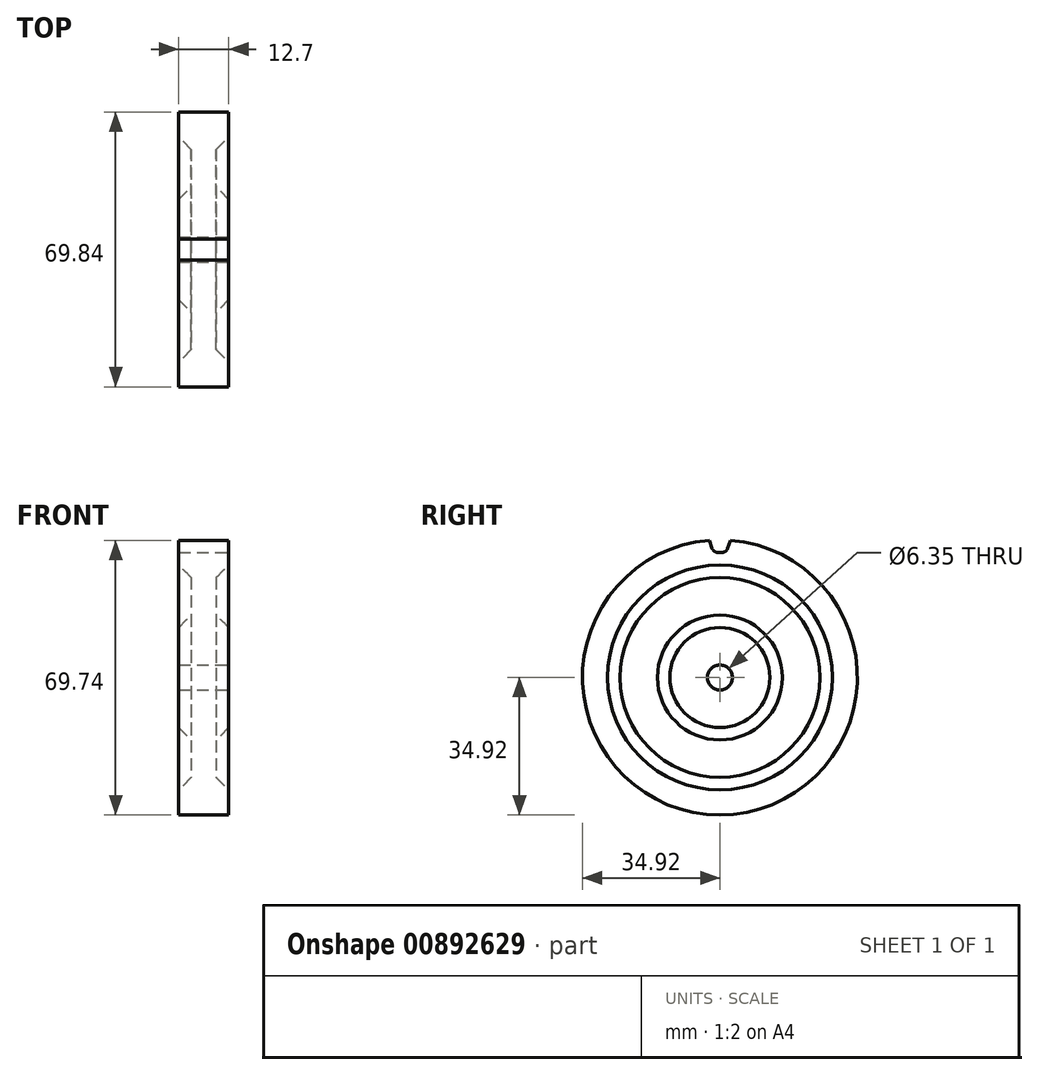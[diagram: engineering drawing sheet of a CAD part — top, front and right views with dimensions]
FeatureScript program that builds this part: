
annotation { "Feature Type Name" : "Feature", "Feature Type Description" : "" }
export const myFeature = defineFeature(function(context is Context, id is Id, definition is map)
    precondition{}
    {
        {
            var Q0;
            Q0=qCreatedBy(makeId("Front.planeOp"),FACE);
            var sketch = newSketch(context, id + "F0", { "sketchPlane" : qUnion([Q0])});
            skLineSegment(sketch, "E0", {"start": v(0, -32.59) * mm, "end": v(0, 41.72) * mm, "construction": true});
            skLineSegment(sketch, "E1", {"start": v(0, 34.93) * mm, "end": v(6.35, 34.93) * mm});
            skLineSegment(sketch, "E2", {"start": v(6.35, 34.93) * mm, "end": v(6.35, 28.58) * mm});
            skLineSegment(sketch, "E3", {"start": v(6.35, 28.58) * mm, "end": v(3.17, 25.4) * mm});
            skLineSegment(sketch, "E4", {"start": v(3.17, 25.4) * mm, "end": v(3.17, 15.88) * mm});
            skLineSegment(sketch, "E5", {"start": v(3.17, 15.88) * mm, "end": v(6.35, 12.7) * mm});
            skLineSegment(sketch, "E6", {"start": v(6.35, 12.7) * mm, "end": v(6.35, 0) * mm});
            skLineSegment(sketch, "E7", {"start": v(-34.52, 0) * mm, "end": v(33.25, 0) * mm, "construction": true});
            skLineSegment(sketch, "E8.MirrorCS", {"start": v(-6.35, 12.7) * mm, "end": v(-6.35, 0) * mm});
            skLineSegment(sketch, "E9.MirrorCS", {"start": v(-6.35, 34.93) * mm, "end": v(-6.35, 28.58) * mm});
            skLineSegment(sketch, "E10.MirrorCS", {"start": v(-3.17, 25.4) * mm, "end": v(-3.17, 15.88) * mm});
            skLineSegment(sketch, "E11.MirrorCS", {"start": v(-6.35, 28.58) * mm, "end": v(-3.17, 25.4) * mm});
            skLineSegment(sketch, "E12.MirrorCS", {"start": v(-3.17, 15.88) * mm, "end": v(-6.35, 12.7) * mm});
            skLineSegment(sketch, "E13.MirrorCS", {"start": v(0, 34.93) * mm, "end": v(-6.35, 34.93) * mm});
            skLineSegment(sketch, "E14", {"start": v(-6.35, 0) * mm, "end": v(6.35, 0) * mm});
            skSolve(sketch);
        }
        {
            var Q0;
            Q0=qSketchRegion(id+"F0",true);
            var Q1;
            Q1=sQuery(id+"F0.wireOp",EDGE,"E7");
            revolve(context, id + "F1", {"surfaceOperationType" : NewSurfaceOperationType.NEW, "entities" : qUnion([Q0]), "axis" : qUnion([Q1]), "revolveType" : RevolveType.FULL});
        }
        {
            var Q0;
            Q0=makeQuery(id+"F1.opRevolve","SWEPT_FACE",FACE,{"disambiguationData":[OSD([sQuery(id+"F0.wireOp",EDGE,"E6")])]});
            var sketch = newSketch(context, id + "F2", { "sketchPlane" : qUnion([Q0])});
            skCircle(sketch, "E15", {"center": v(0, 0) * mm, "radius": 3.18 * mm});
            skSolve(sketch);
        }
        {
            var Q0;
            Q0=makeQuery(id+"F2.imprint","IMPRINT",FACE,{"disambiguationData":[TD([[makeQuery(id+"F2.imprint","IMPRINT",EDGE,{"derivedFrom":sQuery(id+"F2.wireOp",EDGE,"E15")}),1.0]])]});
            extrude(context, id + "F3", {"entities" : qUnion([Q0]), "operationType" : NewBodyOperationType.REMOVE, "endBound" : BoundingType.THROUGH_ALL, "oppositeDirection" : true, "depth" : 25.4 * mm, "offsetDistance" : 25.4 * mm});
        }
        {
            var Q0;
            Q0=makeQuery(id+"F1.opRevolve","SWEPT_FACE",FACE,{"disambiguationData":[OSD([sQuery(id+"F0.wireOp",EDGE,"E2")])]});
            var sketch = newSketch(context, id + "F4", { "sketchPlane" : qUnion([Q0])});
            skLineSegment(sketch, "E16", {"start": v(0, 0) * mm, "end": v(0, 48.24) * mm, "construction": true});
            skArc(sketch, "E17.0", {"start": v(2.7, 34.82) * mm, "mid": v(0, 34.92) * mm, "end": v(-2.7, 34.82) * mm});
            skLineSegment(sketch, "E18", {"start": v(2.7, 34.82) * mm, "end": v(1.59, 31.75) * mm});
            skLineSegment(sketch, "E19", {"start": v(1.59, 31.75) * mm, "end": v(0, 31.75) * mm});
            skLineSegment(sketch, "E20.MirrorCS", {"start": v(-1.59, 31.75) * mm, "end": v(0, 31.75) * mm});
            skLineSegment(sketch, "E21.MirrorCS", {"start": v(-2.7, 34.82) * mm, "end": v(-1.59, 31.75) * mm});
            skSolve(sketch);
        }
        {
            var Q0;
            Q0=qSketchRegion(id+"F4",true);
            extrude(context, id + "F5", {"entities" : qUnion([Q0]), "operationType" : NewBodyOperationType.REMOVE, "endBound" : BoundingType.THROUGH_ALL, "oppositeDirection" : true, "depth" : 25.4 * mm, "offsetDistance" : 25.4 * mm});
        }
        {
            var Q0;
            Q0=makeQuery(id+"F5.boolean.opBoolean","COPY",EDGE,{"derivedFrom":makeQuery(id+"F5.opExtrude","SWEPT_EDGE",EDGE,{"disambiguationData":[OSD([sQuery(id+"F4.wireOp",EDGE,"E20.MirrorCS"),sQuery(id+"F4.wireOp",EDGE,"E21.MirrorCS")])]})});
            var Q1;
            Q1=makeQuery(id+"F5.boolean.opBoolean","COPY",EDGE,{"derivedFrom":makeQuery(id+"F5.opExtrude","SWEPT_EDGE",EDGE,{"disambiguationData":[OSD([sQuery(id+"F4.wireOp",EDGE,"E18"),sQuery(id+"F4.wireOp",EDGE,"E19")])]})});
            var Q2;
            Q2=makeQuery(id+"F5.boolean.opBoolean","COPY",EDGE,{"derivedFrom":makeQuery(id+"F5.opExtrude","SWEPT_EDGE",EDGE,{"disambiguationData":[OSD([sQuery(id+"F0.wireOp",EDGE,"E1"),sQuery(id+"F0.wireOp",EDGE,"E2"),sQuery(id+"F4.wireOp",EDGE,"E17.0"),sQuery(id+"F4.wireOp",EDGE,"E18")])]})});
            var Q3;
            Q3=makeQuery(id+"F5.boolean.opBoolean","COPY",EDGE,{"derivedFrom":makeQuery(id+"F5.opExtrude","SWEPT_EDGE",EDGE,{"disambiguationData":[OSD([sQuery(id+"F0.wireOp",EDGE,"E1"),sQuery(id+"F0.wireOp",EDGE,"E2"),sQuery(id+"F4.wireOp",EDGE,"E17.0"),sQuery(id+"F4.wireOp",EDGE,"E21.MirrorCS")])]})});
            fillet(context, id + "F6", {"entities" : qUnion([Q0, Q1, Q2, Q3]), "radius" : 1.59 * mm, "tangentPropagation" : true, "allowEdgeOverflow" : false});
        }
    });
